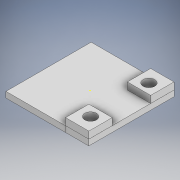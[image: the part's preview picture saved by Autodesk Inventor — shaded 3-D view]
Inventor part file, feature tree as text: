
AUTODESK INVENTOR PART (.ipt)
format: ipt  version: 2020 (Build 240168000, 168)  size: 149,504 bytes
history: native  units: mm
features: sketch x6, extrude x5
ambient origin geometry x8: Origin, YZ Plane, XZ Plane, XY Plane, X Axis, Y Axis, Z Axis, Center Point
bodies: Solid1 (feature_tree)
feature tree (11):
  sketch  "Sketch1"  dims[d4=10.0mm d6=2.0mm]
  sketch  "Sketch2"  dims[d7=2.0mm d8=2.3mm]
  extrude  "Extrusion1"  Depth=10.0mm
  extrude  "Extrusion2"  Depth=2.3mm
  extrude  "Extrusion3"  Depth=7.3mm
  sketch  "Sketch4"  dims[d14=1.7mm d15=1.7mm]
  extrude  "Extrusion4"  Depth=1.7mm
  extrude  "Extrusion5"  Depth=1.0mm TaperAngle=0.0deg
  sketch  "Sketch3"  dims[d9=14.2mm d10=7.3mm]
  sketch  "Sketch5"  dims[d16=1.2mm d17=0.0mm d18=1.0mm d19=0.0mm]
  sketch  "Sketch6"  dims[d20=4.0mm d21=0.0mm d22=2.0mm d23=1.0mm d24=0.0mm d25=2.0mm d26=1.0mm d27=0.0mm]
